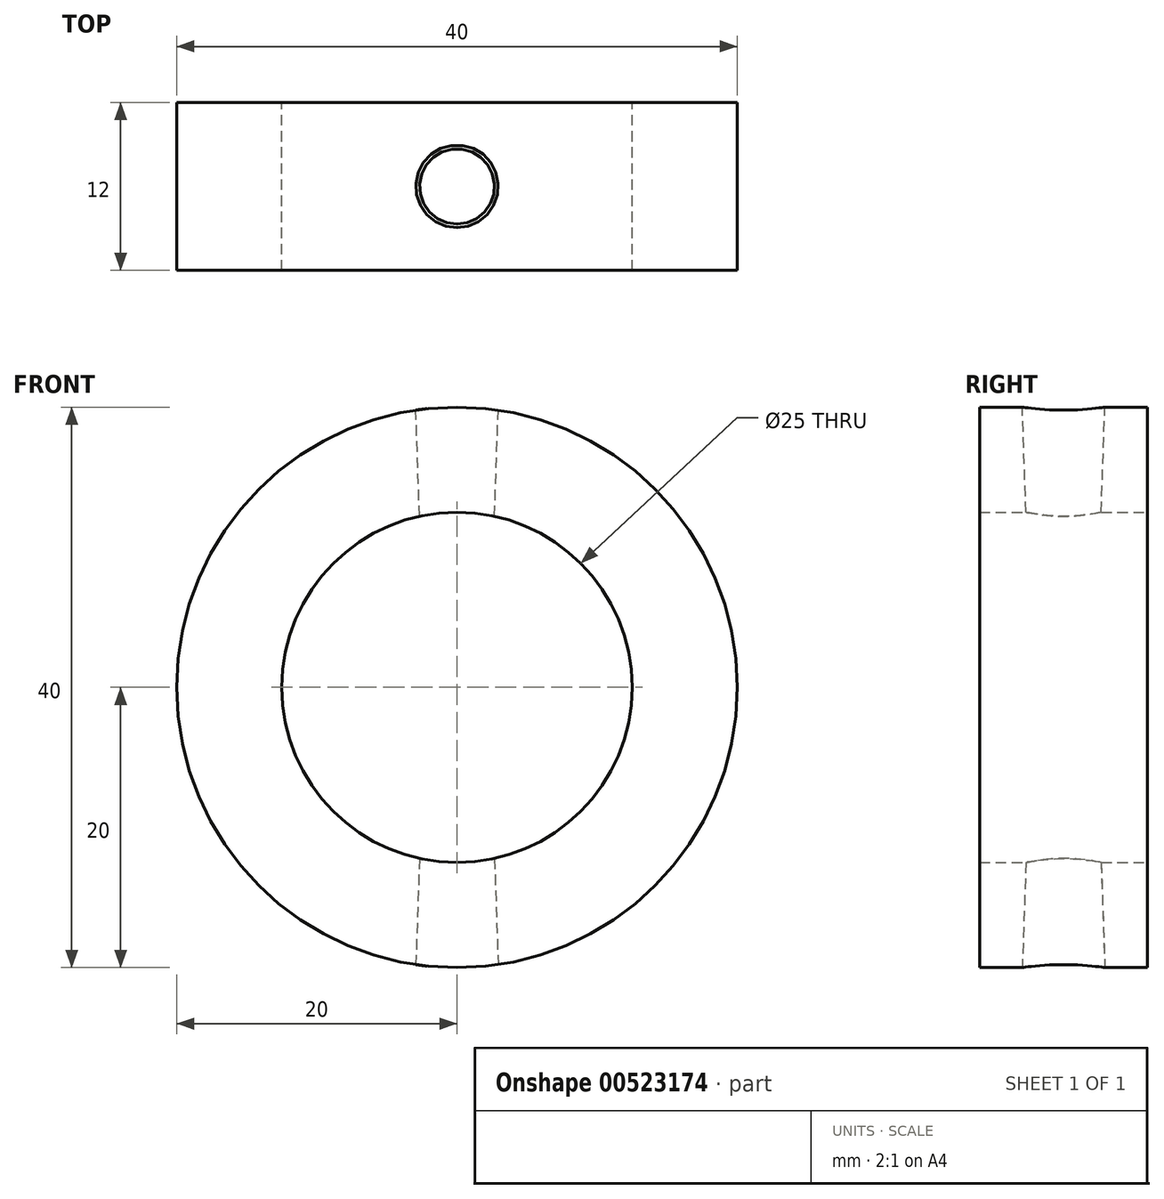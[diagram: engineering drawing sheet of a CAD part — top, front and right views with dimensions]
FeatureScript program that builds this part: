
annotation { "Feature Type Name" : "Feature", "Feature Type Description" : "" }
export const myFeature = defineFeature(function(context is Context, id is Id, definition is map)
    precondition{}
    {
        {
            var Q0;
            Q0=qCreatedBy(makeId("Front.planeOp"),FACE);
            var sketch = newSketch(context, id + "F0", { "sketchPlane" : qUnion([Q0])});
            skCircle(sketch, "E0", {"center": v(0, 0) * mm, "radius": 20 * mm});
            skCircle(sketch, "E1", {"center": v(0, 0) * mm, "radius": 12.5 * mm});
            skSolve(sketch);
        }
        {
            var Q0;
            Q0 = qSketchRegion(id + "F0", true);
            extrude(context, id + "F1", {"entities" : qUnion([Q0]), "endBound" : BoundingType.SYMMETRIC, "depth" : 12 * mm, "offsetDistance" : 25 * mm});
        }
        {
            var Q0;
            Q0=qCreatedBy(makeId("Top.planeOp"),FACE);
            var sketch = newSketch(context, id + "F2", { "sketchPlane" : qUnion([Q0])});
            skCircle(sketch, "E2", {"center": v(0, 0) * mm, "radius": 2.25 * mm});
            skSolve(sketch);
        }
        {
            var Q0;
            Q0 = qSketchRegion(id + "F2", true);
            extrude(context, id + "F3", {"entities" : qUnion([Q0]), "operationType" : NewBodyOperationType.REMOVE, "endBound" : BoundingType.SYMMETRIC, "depth" : 50 * mm, "offsetDistance" : 25 * mm, "hasDraft" : true, "draftAngle" : 2 * degree});
        }
    });
